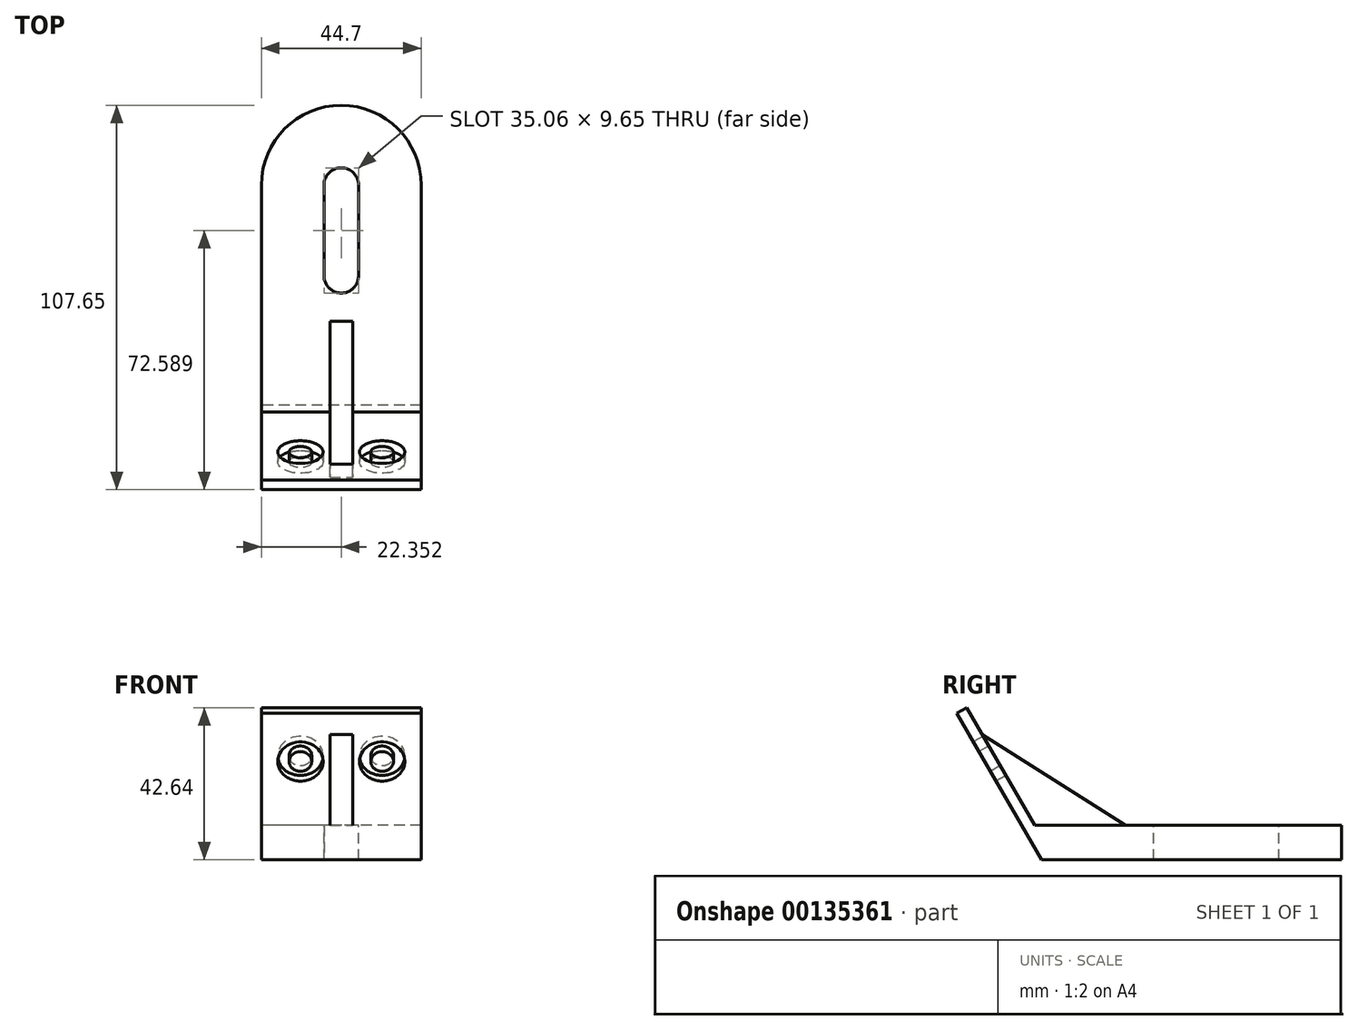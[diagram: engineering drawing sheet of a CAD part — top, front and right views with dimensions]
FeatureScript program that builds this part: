
annotation { "Feature Type Name" : "Feature", "Feature Type Description" : "" }
export const myFeature = defineFeature(function(context is Context, id is Id, definition is map)
    precondition{}
    {
        {
            var Q0;
            Q0=qCreatedBy(makeId("Right.planeOp"),FACE);
            var sketch = newSketch(context, id + "F0", { "sketchPlane" : qUnion([Q0])});
            skLineSegment(sketch, "E0", {"start": v(-34.53, 10.94) * mm, "end": v(28.97, 10.94) * mm});
            skLineSegment(sketch, "E1", {"start": v(28.97, 10.94) * mm, "end": v(28.97, 1.29) * mm});
            skLineSegment(sketch, "E2", {"start": v(28.97, 1.29) * mm, "end": v(-32.62, 1.29) * mm});
            skLineSegment(sketch, "E3", {"start": v(-34.53, 10.94) * mm, "end": v(-53.58, 43.93) * mm});
            skLineSegment(sketch, "E4", {"start": v(-53.58, 43.93) * mm, "end": v(-56.32, 42.35) * mm});
            skLineSegment(sketch, "E5", {"start": v(-56.32, 42.35) * mm, "end": v(-32.62, 1.29) * mm});
            skSolve(sketch);
        }
        {
            var Q0;
            Q0 = qSketchRegion(id + "F0", true);
            extrude(context, id + "F1", {"entities" : qUnion([Q0]), "depth" : 44.7 * mm});
        }
        {
            var Q0;
            Q0=makeQuery(id+"F1.opExtrude","SWEPT_FACE",FACE,{"disambiguationData":[OSD([sQuery(id+"F0.wireOp",EDGE,"E0")])]});
            var sketch = newSketch(context, id + "F2", { "sketchPlane" : qUnion([Q0])});
            skArc(sketch, "E6", {"start": v(44.7, 28.97) * mm, "mid": v(22.35, 51.33) * mm, "end": v(0, 28.97) * mm});
            skLineSegment(sketch, "E7", {"start": v(0, 28.97) * mm, "end": v(0, -34.53) * mm});
            skLineSegment(sketch, "E8", {"start": v(0, -34.53) * mm, "end": v(19.18, -34.53) * mm});
            skLineSegment(sketch, "E9", {"start": v(19.18, -34.53) * mm, "end": v(19.18, -9.13) * mm});
            skLineSegment(sketch, "E10", {"start": v(19.18, -9.13) * mm, "end": v(25.53, -9.13) * mm});
            skLineSegment(sketch, "E11", {"start": v(25.53, -9.13) * mm, "end": v(25.53, -34.53) * mm});
            skLineSegment(sketch, "E12", {"start": v(25.53, -34.53) * mm, "end": v(44.7, -34.53) * mm});
            skLineSegment(sketch, "E13", {"start": v(19.18, -34.53) * mm, "end": v(19.18, -53.6) * mm});
            skLineSegment(sketch, "E14", {"start": v(25.53, -34.53) * mm, "end": v(25.53, -53.75) * mm});
            skLineSegment(sketch, "E15", {"start": v(25.53, -53.75) * mm, "end": v(19.18, -53.6) * mm});
            skLineSegment(sketch, "E16", {"start": v(44.7, -34.53) * mm, "end": v(44.7, 28.97) * mm});
            skLineSegment(sketch, "E17", {"start": v(0, 28.97) * mm, "end": v(44.7, 28.97) * mm});
            skLineSegment(sketch, "E18", {"start": v(17.53, 28.97) * mm, "end": v(17.53, 3.57) * mm});
            skLineSegment(sketch, "E19", {"start": v(27.18, 28.97) * mm, "end": v(27.18, 3.57) * mm});
            skArc(sketch, "E20", {"start": v(27.18, 28.97) * mm, "mid": v(22.35, 33.8) * mm, "end": v(17.53, 28.97) * mm});
            skArc(sketch, "E21", {"start": v(17.53, 3.57) * mm, "mid": v(22.35, -1.26) * mm, "end": v(27.18, 3.57) * mm});
            skLineSegment(sketch, "E22", {"start": v(17.53, 3.57) * mm, "end": v(22.35, 3.56) * mm});
            skLineSegment(sketch, "E23", {"start": v(22.35, 3.56) * mm, "end": v(27.18, 3.57) * mm});
            skSolve(sketch);
        }
        {
            var Q0;
            Q0=makeQuery(id+"F1.opExtrude","SWEPT_FACE",FACE,{"disambiguationData":[OSD([sQuery(id+"F0.wireOp",EDGE,"E5")])]});
            var sketch = newSketch(context, id + "F3", { "sketchPlane" : qUnion([Q0])});
            skCircle(sketch, "E24", {"center": v(10.92, 49.25) * mm, "radius": 3.18 * mm});
            skCircle(sketch, "E25", {"center": v(33.78, 49.25) * mm, "radius": 3.18 * mm});
            skLineSegment(sketch, "E26", {"start": v(10.92, 49.25) * mm, "end": v(0, 49.25) * mm, "construction": true});
            skLineSegment(sketch, "E27", {"start": v(33.78, 49.25) * mm, "end": v(44.7, 49.25) * mm, "construction": true});
            skCircle(sketch, "E28", {"center": v(10.92, 49.25) * mm, "radius": 6.35 * mm});
            skCircle(sketch, "E29", {"center": v(33.78, 49.25) * mm, "radius": 6.35 * mm});
            skSolve(sketch);
        }
        {
            var Q0;
            Q0=makeQuery(id+"F3.imprint","IMPRINT",FACE,{"disambiguationData":[TD([[makeQuery(id+"F3.imprint","IMPRINT",EDGE,{"derivedFrom":sQuery(id+"F3.wireOp",EDGE,"E24")}),-1.0]])]});
            var Q1;
            Q1=makeQuery(id+"F3.imprint","IMPRINT",FACE,{"disambiguationData":[TD([[makeQuery(id+"F3.imprint","IMPRINT",EDGE,{"derivedFrom":sQuery(id+"F3.wireOp",EDGE,"E25")}),-1.0]])]});
            extrude(context, id + "F4", {"entities" : qUnion([Q0, Q1]), "operationType" : NewBodyOperationType.REMOVE, "oppositeDirection" : true, "depth" : 3.17 * mm});
        }
        {
            var Q0;
            {var subQ0=sQuery(id+"F2.wireOp",EDGE,"E6");Q0=makeQuery(id+"F2.imprint","IMPRINT",FACE,{"disambiguationData":[TD([[makeQuery(id+"F2.imprint","IMPRINT",EDGE,{"derivedFrom":subQ0}),1.0]])]});}
            extrude(context, id + "F5", {"entities" : qUnion([Q0]), "operationType" : NewBodyOperationType.ADD, "oppositeDirection" : true, "depth" : 9.65 * mm});
        }
        {
            var Q0;
            {var subQ0=sQuery(id+"F2.wireOp",EDGE,"E13");Q0=makeQuery(id+"F2.imprint","IMPRINT",FACE,{"disambiguationData":[TD([[makeQuery(id+"F2.imprint","IMPRINT",EDGE,{"derivedFrom":subQ0}),1.0]])]});}
            extrude(context, id + "F6", {"entities" : qUnion([Q0]), "operationType" : NewBodyOperationType.ADD, "depth" : 25.4 * mm});
        }
        {
            var Q0;
            {var subQ0=sQuery(id+"F2.wireOp",EDGE,"E9");Q0=makeQuery(id+"F2.imprint","IMPRINT",FACE,{"disambiguationData":[TD([[makeQuery(id+"F2.imprint","IMPRINT",EDGE,{"derivedFrom":subQ0}),-1.0]])]});}
            extrude(context, id + "F7", {"entities" : qUnion([Q0]), "operationType" : NewBodyOperationType.ADD, "depth" : 25.4 * mm});
        }
        {
            var Q0;
            Q0=makeQuery(id+"F2.imprint","IMPRINT",FACE,{"disambiguationData":[TD([[makeQuery(id+"F2.imprint","IMPRINT",EDGE,{"derivedFrom":sQuery(id+"F2.wireOp",EDGE,"E21")}),1.0]])]});
            extrude(context, id + "F8", {"entities" : qUnion([Q0]), "operationType" : NewBodyOperationType.REMOVE, "oppositeDirection" : true, "depth" : 25.4 * mm});
        }
        {
            var Q0;
            {var subQ1=sQuery(id+"F2.wireOp",EDGE,"E18");Q0=makeQuery(id+"F2.imprint","IMPRINT",FACE,{"disambiguationData":[TD([[makeQuery(id+"F2.imprint","IMPRINT",EDGE,{"derivedFrom":subQ1}),1.0]])]});}
            extrude(context, id + "F9", {"entities" : qUnion([Q0]), "operationType" : NewBodyOperationType.REMOVE, "oppositeDirection" : true, "depth" : 25.4 * mm});
        }
        {
            var Q0;
            {var subQ0=sQuery(id+"F2.wireOp",EDGE,"E14");var subQ2=sQuery(id+"F0.wireOp",EDGE,"E0");Q0=makeQuery(id+"F7.boolean.opBoolean","MERGE",FACE,{"derivedFrom":[makeQuery(id+"F6.boolean.opBoolean","SPLIT",FACE,{"disambiguationData":[TD([makeQuery(id+"F1.opExtrude","SWEPT_FACE",FACE,{"disambiguationData":[OSD([subQ2])]})])],"derivedFrom":makeQuery(id+"F6.opExtrude","SWEPT_FACE",FACE,{"disambiguationData":[OSD([subQ0])]})}),makeQuery(id+"F7.opExtrude","SWEPT_FACE",FACE,{"disambiguationData":[OSD([sQuery(id+"F2.wireOp",EDGE,"E11")])]})]});}
            var sketch = newSketch(context, id + "F10", { "sketchPlane" : qUnion([Q0])});
            skLineSegment(sketch, "E30", {"start": v(-49.2, 36.34) * mm, "end": v(-9.13, 10.94) * mm});
            skLineSegment(sketch, "E31", {"start": v(-9.13, 10.94) * mm, "end": v(-34.53, 10.94) * mm});
            skLineSegment(sketch, "E32", {"start": v(-34.53, 10.94) * mm, "end": v(-49.2, 36.34) * mm});
            skLineSegment(sketch, "E33", {"start": v(-49.2, 36.34) * mm, "end": v(-9.13, 36.34) * mm});
            skLineSegment(sketch, "E34", {"start": v(-9.13, 36.34) * mm, "end": v(-9.13, 10.94) * mm});
            skSolve(sketch);
        }
        {
            var Q0;
            Q0=makeQuery(id+"F10.imprint","IMPRINT",FACE,{"disambiguationData":[TD([[makeQuery(id+"F10.imprint","IMPRINT",EDGE,{"derivedFrom":sQuery(id+"F10.wireOp",EDGE,"E30")}),1.0]])]});
            extrude(context, id + "F11", {"entities" : qUnion([Q0]), "operationType" : NewBodyOperationType.REMOVE, "oppositeDirection" : true, "depth" : 25.4 * mm});
        }
        {
            var Q0;
            {var subQ1=sQuery(id+"F2.wireOp",EDGE,"E14");Q0=makeQuery(id+"F6.boolean.opBoolean","SPLIT",FACE,{"disambiguationData":[TD([makeQuery(id+"F1.opExtrude","SWEPT_FACE",FACE,{"disambiguationData":[OSD([sQuery(id+"F0.wireOp",EDGE,"E5")])]})])],"derivedFrom":makeQuery(id+"F6.opExtrude","SWEPT_FACE",FACE,{"disambiguationData":[OSD([subQ1])]})});}
            var sketch = newSketch(context, id + "F12", { "sketchPlane" : qUnion([Q0])});
            skLineSegment(sketch, "E35", {"start": v(-53.75, 36.34) * mm, "end": v(-53.75, 10.94) * mm});
            skLineSegment(sketch, "E36", {"start": v(-53.75, 10.94) * mm, "end": v(-38.2, 10.94) * mm});
            skLineSegment(sketch, "E37", {"start": v(-38.2, 10.94) * mm, "end": v(-52.99, 36.5) * mm});
            skLineSegment(sketch, "E38", {"start": v(-53.75, 36.34) * mm, "end": v(-52.86, 36.34) * mm});
            skSolve(sketch);
        }
        {
            var Q0;
            Q0 = qSketchRegion(id + "F12", true);
            extrude(context, id + "F13", {"entities" : qUnion([Q0]), "operationType" : NewBodyOperationType.REMOVE, "oppositeDirection" : true, "depth" : 25.4 * mm});
        }
    });
